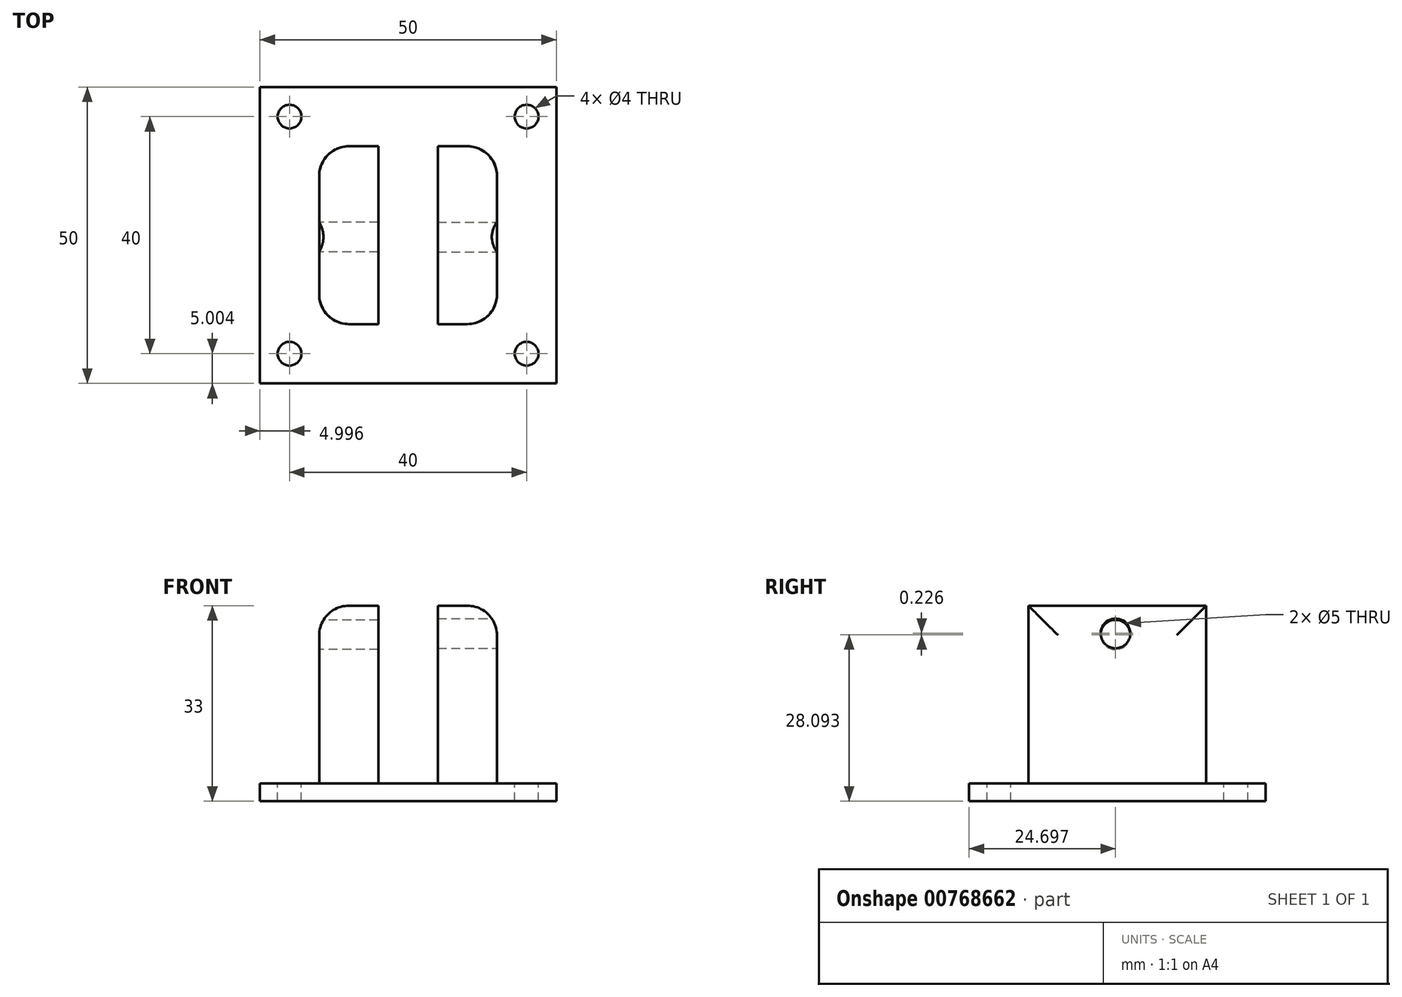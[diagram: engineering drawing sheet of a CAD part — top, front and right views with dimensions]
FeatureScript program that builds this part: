
annotation { "Feature Type Name" : "Feature", "Feature Type Description" : "" }
export const myFeature = defineFeature(function(context is Context, id is Id, definition is map)
    precondition{}
    {
        {
            var Q0;
            Q0=qCreatedBy(makeId("Top.planeOp"),FACE);
            var sketch = newSketch(context, id + "F0", { "sketchPlane" : qUnion([Q0])});
            skLineSegment(sketch, "E0.bottom", {"start": v(-24.77, -18.04) * mm, "end": v(25.23, -18.04) * mm});
            skLineSegment(sketch, "E0.top", {"start": v(-24.77, 31.96) * mm, "end": v(25.23, 31.96) * mm});
            skLineSegment(sketch, "E0.left", {"start": v(-24.77, -18.04) * mm, "end": v(-24.77, 31.96) * mm});
            skLineSegment(sketch, "E0.right", {"start": v(25.23, -18.04) * mm, "end": v(25.23, 31.96) * mm});
            skSolve(sketch);
        }
        {
            var Q0;
            Q0 = qSketchRegion(id + "F0", true);
            extrude(context, id + "F1", {"entities" : qUnion([Q0]), "depth" : 3 * mm, "offsetDistance" : 25 * mm});
        }
        {
            var Q0;
            Q0=makeQuery(id+"F1.opExtrude","CAP_FACE",FACE,{"disambiguationData":[OSD([sQuery(id+"F0.wireOp",EDGE,"E0.bottom"),sQuery(id+"F0.wireOp",EDGE,"E0.top"),sQuery(id+"F0.wireOp",EDGE,"E0.left"),sQuery(id+"F0.wireOp",EDGE,"E0.right")])],"isStart":false});
            var sketch = newSketch(context, id + "F2", { "sketchPlane" : qUnion([Q0])});
            skLineSegment(sketch, "E1.bottom", {"start": v(-14.77, 21.96) * mm, "end": v(-4.77, 21.96) * mm});
            skLineSegment(sketch, "E1.top", {"start": v(-14.77, -8.04) * mm, "end": v(-4.77, -8.04) * mm});
            skLineSegment(sketch, "E1.left", {"start": v(-14.77, 21.96) * mm, "end": v(-14.77, -8.04) * mm});
            skLineSegment(sketch, "E1.right", {"start": v(-4.77, 21.96) * mm, "end": v(-4.77, -8.04) * mm});
            skLineSegment(sketch, "E2.bottom", {"start": v(5.23, 21.96) * mm, "end": v(15.23, 21.96) * mm});
            skLineSegment(sketch, "E2.top", {"start": v(5.23, -8.04) * mm, "end": v(15.23, -8.04) * mm});
            skLineSegment(sketch, "E2.left", {"start": v(5.23, 21.96) * mm, "end": v(5.23, -8.04) * mm});
            skLineSegment(sketch, "E2.right", {"start": v(15.23, 21.96) * mm, "end": v(15.23, -8.04) * mm});
            skSolve(sketch);
        }
        {
            var Q0;
            Q0 = qSketchRegion(id + "F2", true);
            extrude(context, id + "F3", {"entities" : qUnion([Q0]), "operationType" : NewBodyOperationType.ADD, "depth" : 30 * mm, "offsetDistance" : 25 * mm});
        }
        {
            var Q0;
            Q0=makeQuery(id+"F3.opExtrude","SWEPT_FACE",FACE,{"disambiguationData":[OSD([sQuery(id+"F2.wireOp",EDGE,"E2.right")])]});
            var sketch = newSketch(context, id + "F4", { "sketchPlane" : qUnion([Q0])});
            skCircle(sketch, "E3", {"center": v(6.66, 28.32) * mm, "radius": 2.5 * mm});
            skSolve(sketch);
        }
        {
            var Q0;
            Q0 = qSketchRegion(id + "F4", true);
            extrude(context, id + "F5", {"entities" : qUnion([Q0]), "operationType" : NewBodyOperationType.REMOVE, "oppositeDirection" : true, "depth" : 10 * mm, "offsetDistance" : 25 * mm});
        }
        {
            var Q0;
            Q0=makeQuery(id+"F3.opExtrude","SWEPT_FACE",FACE,{"disambiguationData":[OSD([sQuery(id+"F2.wireOp",EDGE,"E1.left")])]});
            var sketch = newSketch(context, id + "F6", { "sketchPlane" : qUnion([Q0])});
            skCircle(sketch, "E4", {"center": v(-6.66, 28.1) * mm, "radius": 2.5 * mm});
            skSolve(sketch);
        }
        {
            var Q0;
            Q0 = qSketchRegion(id + "F6", true);
            extrude(context, id + "F7", {"entities" : qUnion([Q0]), "operationType" : NewBodyOperationType.REMOVE, "oppositeDirection" : true, "depth" : 10 * mm, "offsetDistance" : 25 * mm});
        }
        {
            var Q0;
            Q0=makeQuery(id+"F3.opExtrude","SWEPT_EDGE",EDGE,{"disambiguationData":[OSD([sQuery(id+"F2.wireOp",EDGE,"E1.bottom"),sQuery(id+"F2.wireOp",EDGE,"E1.left")])]});
            var Q1;
            Q1=makeQuery(id+"F3.opExtrude","CAP_EDGE",EDGE,{"disambiguationData":[OSD([sQuery(id+"F2.wireOp",EDGE,"E1.left")])],"isStart":false});
            var Q2;
            Q2=makeQuery(id+"F3.opExtrude","SWEPT_EDGE",EDGE,{"disambiguationData":[OSD([sQuery(id+"F2.wireOp",EDGE,"E1.top"),sQuery(id+"F2.wireOp",EDGE,"E1.left")])]});
            var Q3;
            Q3=makeQuery(id+"F7.boolean.opBoolean","COPY",EDGE,{"derivedFrom":makeQuery(id+"F7.opExtrude","CAP_EDGE",EDGE,{"disambiguationData":[OSD([sQuery(id+"F6.wireOp",EDGE,"E4")])],"isStart":true})});
            fillet(context, id + "F8", {"entities" : qUnion([Q0, Q1, Q2, Q3]), "radius" : 5 * mm, "tangentPropagation" : true, "allowEdgeOverflow" : false});
        }
        {
            var Q0;
            Q0=makeQuery(id+"F3.opExtrude","SWEPT_EDGE",EDGE,{"disambiguationData":[OSD([sQuery(id+"F2.wireOp",EDGE,"E2.top"),sQuery(id+"F2.wireOp",EDGE,"E2.right")])]});
            var Q1;
            Q1=makeQuery(id+"F3.opExtrude","CAP_EDGE",EDGE,{"disambiguationData":[OSD([sQuery(id+"F2.wireOp",EDGE,"E2.right")])],"isStart":false});
            var Q2;
            Q2=makeQuery(id+"F3.opExtrude","SWEPT_EDGE",EDGE,{"disambiguationData":[OSD([sQuery(id+"F2.wireOp",EDGE,"E2.bottom"),sQuery(id+"F2.wireOp",EDGE,"E2.right")])]});
            var Q3;
            Q3=makeQuery(id+"F5.boolean.opBoolean","COPY",EDGE,{"derivedFrom":makeQuery(id+"F5.opExtrude","CAP_EDGE",EDGE,{"disambiguationData":[OSD([sQuery(id+"F4.wireOp",EDGE,"E3")])],"isStart":true})});
            fillet(context, id + "F9", {"entities" : qUnion([Q0, Q1, Q2, Q3]), "radius" : 5 * mm, "tangentPropagation" : true, "allowEdgeOverflow" : false});
        }
        {
            var Q0;
            Q0=makeQuery(id+"F2.imprint","IMPRINT",FACE,{"disambiguationData":[TD([[makeQuery(id+"F2.imprint","IMPRINT",EDGE,{"derivedFrom":sQuery(id+"F2.wireOp",EDGE,"E1.bottom")}),1.0]])]});
            var sketch = newSketch(context, id + "F10", { "sketchPlane" : qUnion([Q0])});
            skPoint(sketch, "E5", {"position": v(-19.77, 26.96) * mm});
            skPoint(sketch, "E6", {"position": v(20.23, 26.96) * mm});
            skPoint(sketch, "E7", {"position": v(20.23, -13.04) * mm});
            skPoint(sketch, "E8", {"position": v(-19.77, -13.04) * mm});
            skSolve(sketch);
        }
        {
            var Q0;
            Q0=sQuery(id+"F10.wireOp",VERTEX,"E6");
            var Q1;
            Q1=sQuery(id+"F10.wireOp",VERTEX,"E5");
            var Q2;
            Q2=sQuery(id+"F10.wireOp",VERTEX,"E8");
            var Q3;
            Q3=sQuery(id+"F10.wireOp",VERTEX,"E7");
            var Q4;
            Q4=makeQuery(id+"F1.opExtrude","SWEPT_BODY",BODY,{"disambiguationData":[OSD([sQuery(id+"F0.wireOp",EDGE,"E0.bottom"),sQuery(id+"F0.wireOp",EDGE,"E0.top"),sQuery(id+"F0.wireOp",EDGE,"E0.left"),sQuery(id+"F0.wireOp",EDGE,"E0.right")])]});
            hole(context, id + "F11", {"style" : HoleStyle.SIMPLE, "endStyle" : HoleEndStyle.THROUGH, "holeDiameter" : 4 * mm, "majorDiameter" : 5 * mm, "isTappedThrough" : true, "tappedDepth" : 12 * mm, "tapClearance" : 3, "locations" : qUnion([Q0, Q1, Q2, Q3]), "scope" : qUnion([Q4])});
        }
    });
